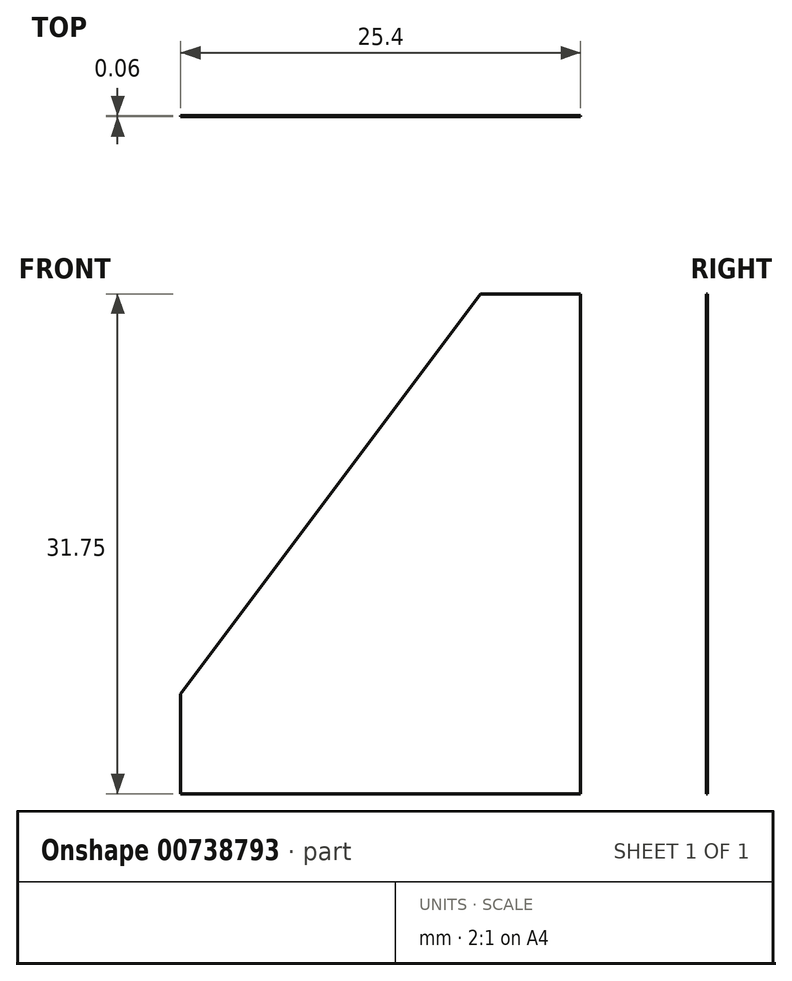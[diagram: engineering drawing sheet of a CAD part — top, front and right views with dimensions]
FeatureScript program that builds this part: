
annotation { "Feature Type Name" : "Feature", "Feature Type Description" : "" }
export const myFeature = defineFeature(function(context is Context, id is Id, definition is map)
    precondition{}
    {
        {
            var Q0;
            Q0=qCreatedBy(makeId("Front.planeOp"),FACE);
            var sketch = newSketch(context, id + "F0", { "sketchPlane" : qUnion([Q0])});
            skLineSegment(sketch, "E0.bottom", {"start": v(-12.7, 36.84) * mm, "end": v(12.7, 36.84) * mm});
            skLineSegment(sketch, "E0.top", {"start": v(-12.7, 5.1) * mm, "end": v(12.7, 5.1) * mm});
            skLineSegment(sketch, "E0.left", {"start": v(-12.7, 36.84) * mm, "end": v(-12.7, 5.1) * mm});
            skLineSegment(sketch, "E0.right", {"start": v(12.7, 36.84) * mm, "end": v(12.7, 5.1) * mm});
            skSolve(sketch);
        }
        {
            var Q0;
            Q0 = qSketchRegion(id + "F0", true);
            extrude(context, id + "F1", {"entities" : qUnion([Q0]), "depth" : 6 / 101.6 * mm, "offsetDistance" : 25.4 * mm});
        }
        {
            var Q0;
            Q0=qCreatedBy(makeId("Front.planeOp"),FACE);
            var sketch = newSketch(context, id + "F2", { "sketchPlane" : qUnion([Q0])});
            skLineSegment(sketch, "E1", {"start": v(6.35, 36.84) * mm, "end": v(-12.7, 11.44) * mm});
            skLineSegment(sketch, "E2", {"start": v(-12.7, 11.44) * mm, "end": v(-12.7, 36.84) * mm});
            skLineSegment(sketch, "E3", {"start": v(6.35, 36.84) * mm, "end": v(-12.7, 36.84) * mm});
            skSolve(sketch);
        }
        {
            var Q0;
            Q0 = qSketchRegion(id + "F2", true);
            extrude(context, id + "F3", {"entities" : qUnion([Q0]), "operationType" : NewBodyOperationType.REMOVE, "depth" : 25.4 * mm, "offsetDistance" : 25.4 * mm});
        }
    });
